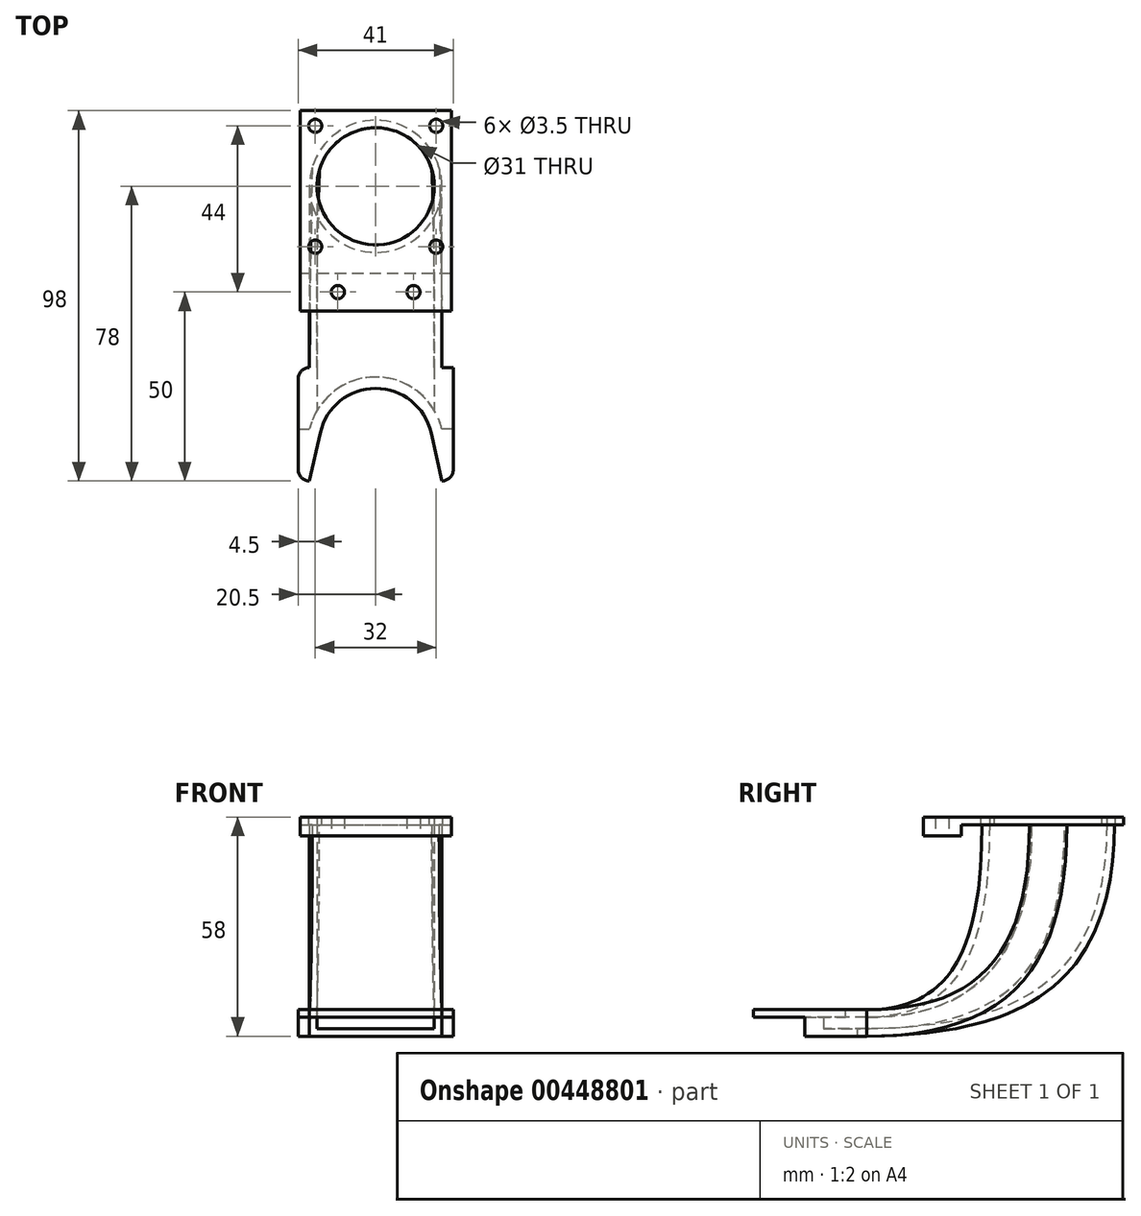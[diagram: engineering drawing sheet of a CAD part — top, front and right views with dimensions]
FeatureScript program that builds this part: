
annotation { "Feature Type Name" : "Feature", "Feature Type Description" : "" }
export const myFeature = defineFeature(function(context is Context, id is Id, definition is map)
    precondition{}
    {
        {
            var Q0;
            Q0=qCreatedBy(makeId("Top.planeOp"),FACE);
            var sketch = newSketch(context, id + "F0", { "sketchPlane" : qUnion([Q0])});
            skLineSegment(sketch, "E0.bottom", {"start": v(0, 0) * mm, "end": v(-40, 0) * mm});
            skLineSegment(sketch, "E0.top", {"start": v(0, 10) * mm, "end": v(-40, 10) * mm});
            skLineSegment(sketch, "E0.left", {"start": v(0, 0) * mm, "end": v(0, 10) * mm});
            skLineSegment(sketch, "E0.right", {"start": v(-40, 0) * mm, "end": v(-40, 10) * mm});
            skCircle(sketch, "E1", {"center": v(-30, 5) * mm, "radius": 1.75 * mm});
            skPoint(sketch, "E1.centerSnap0", {"position": v(-40, 5) * mm});
            skCircle(sketch, "E2", {"center": v(-10, 5) * mm, "radius": 1.75 * mm});
            skPoint(sketch, "E2.centerSnap0", {"position": v(0, 5) * mm});
            skSolve(sketch);
        }
        {
            var Q0;
            Q0=makeQuery(id+"F0.imprint","IMPRINT",FACE,{"disambiguationData":[TD([[makeQuery(id+"F0.imprint","IMPRINT",EDGE,{"derivedFrom":sQuery(id+"F0.wireOp",EDGE,"E0.bottom")}),-1.0]])]});
            extrude(context, id + "F1", {"entities" : qUnion([Q0]), "depth" : 5 * mm});
        }
        {
            var Q0;
            Q0=makeQuery(id+"F1.opExtrude","SWEPT_FACE",FACE,{"disambiguationData":[OSD([sQuery(id+"F0.wireOp",EDGE,"E0.top")])]});
            var sketch = newSketch(context, id + "F2", { "sketchPlane" : qUnion([Q0])});
            skLineSegment(sketch, "E3.bottom", {"start": v(40, 5) * mm, "end": v(0, 5) * mm});
            skLineSegment(sketch, "E3.top", {"start": v(40, 3) * mm, "end": v(0, 3) * mm});
            skLineSegment(sketch, "E3.left", {"start": v(40, 5) * mm, "end": v(40, 3) * mm});
            skLineSegment(sketch, "E3.right", {"start": v(0, 5) * mm, "end": v(0, 3) * mm});
            skSolve(sketch);
        }
        {
            var Q0;
            Q0=makeQuery(id+"F2.imprint","IMPRINT",FACE,{"disambiguationData":[TD([[makeQuery(id+"F2.imprint","IMPRINT",EDGE,{"derivedFrom":sQuery(id+"F2.wireOp",EDGE,"E3.bottom")}),-1.0]])]});
            extrude(context, id + "F3", {"entities" : qUnion([Q0]), "operationType" : NewBodyOperationType.ADD, "depth" : 43 * mm});
        }
        {
            var Q0;
            Q0=makeQuery(id+"F3.boolean.opBoolean","MERGE",FACE,{"derivedFrom":[makeQuery(id+"F1.opExtrude","CAP_FACE",FACE,{"disambiguationData":[OSD([sQuery(id+"F0.wireOp",EDGE,"E0.bottom"),sQuery(id+"F0.wireOp",EDGE,"E0.top"),sQuery(id+"F0.wireOp",EDGE,"E0.left"),sQuery(id+"F0.wireOp",EDGE,"E0.right"),sQuery(id+"F0.wireOp",EDGE,"E1"),sQuery(id+"F0.wireOp",EDGE,"E2")])],"isStart":false}),makeQuery(id+"F3.opExtrude","SWEPT_FACE",FACE,{"disambiguationData":[OSD([sQuery(id+"F2.wireOp",EDGE,"E3.bottom")])]})]});
            var sketch = newSketch(context, id + "F4", { "sketchPlane" : qUnion([Q0])});
            skLineSegment(sketch, "E4.bottom", {"start": v(-36, 49) * mm, "end": v(-4, 49) * mm, "construction": true});
            skLineSegment(sketch, "E4.top", {"start": v(-36, 17) * mm, "end": v(-4, 17) * mm, "construction": true});
            skLineSegment(sketch, "E4.left", {"start": v(-36, 49) * mm, "end": v(-36, 17) * mm, "construction": true});
            skLineSegment(sketch, "E4.right", {"start": v(-4, 49) * mm, "end": v(-4, 17) * mm, "construction": true});
            skPoint(sketch, "E5", {"position": v(-20, 49) * mm});
            skPoint(sketch, "E6", {"position": v(-36, 33) * mm});
            skSolve(sketch);
        }
        {
            var Q0;
            Q0=sQuery(id+"F4.wireOp",VERTEX,"E4.bottom.start");
            var Q1;
            Q1=sQuery(id+"F4.wireOp",VERTEX,"E4.left.end");
            var Q2;
            Q2=sQuery(id+"F4.wireOp",VERTEX,"E4.right.end");
            var Q3;
            Q3=sQuery(id+"F4.wireOp",VERTEX,"E4.right.start");
            var Q4;
            Q4=makeQuery(id+"F1.opExtrude","SWEPT_BODY",BODY,{"disambiguationData":[OSD([sQuery(id+"F0.wireOp",EDGE,"E0.bottom"),sQuery(id+"F0.wireOp",EDGE,"E0.top"),sQuery(id+"F0.wireOp",EDGE,"E0.left"),sQuery(id+"F0.wireOp",EDGE,"E0.right"),sQuery(id+"F0.wireOp",EDGE,"E1"),sQuery(id+"F0.wireOp",EDGE,"E2")])]});
            hole(context, id + "F5", {"style" : HoleStyle.SIMPLE, "endStyle" : HoleEndStyle.THROUGH, "holeDiameter" : 3.5 * mm, "tappedDepth" : 12 * mm, "tapClearance" : 3, "locations" : qUnion([Q0, Q1, Q2, Q3]), "scope" : qUnion([Q4])});
        }
        {
            var Q0;
            Q0=makeQuery(id+"F3.boolean.opBoolean","MERGE",FACE,{"derivedFrom":[makeQuery(id+"F1.opExtrude","CAP_FACE",FACE,{"disambiguationData":[OSD([sQuery(id+"F0.wireOp",EDGE,"E0.bottom"),sQuery(id+"F0.wireOp",EDGE,"E0.top"),sQuery(id+"F0.wireOp",EDGE,"E0.left"),sQuery(id+"F0.wireOp",EDGE,"E0.right"),sQuery(id+"F0.wireOp",EDGE,"E1"),sQuery(id+"F0.wireOp",EDGE,"E2")])],"isStart":false}),makeQuery(id+"F3.opExtrude","SWEPT_FACE",FACE,{"disambiguationData":[OSD([sQuery(id+"F2.wireOp",EDGE,"E3.bottom")])]})]});
            var sketch = newSketch(context, id + "F6", { "sketchPlane" : qUnion([Q0])});
            skCircle(sketch, "E7", {"center": v(-20, 33) * mm, "radius": 17.5 * mm});
            skLineSegment(sketch, "E8", {"start": v(-36, 17) * mm, "end": v(-36, 49) * mm, "construction": true});
            skPoint(sketch, "E9", {"position": v(-36, 33) * mm});
            skSolve(sketch);
        }
        {
            var Q0;
            Q0=makeQuery(id+"F6.imprint","IMPRINT",FACE,{"disambiguationData":[TD([[makeQuery(id+"F6.imprint","IMPRINT",EDGE,{"derivedFrom":sQuery(id+"F6.wireOp",EDGE,"E7")}),1.0]])]});
            extrude(context, id + "F7", {"entities" : qUnion([Q0]), "operationType" : NewBodyOperationType.REMOVE, "endBound" : BoundingType.THROUGH_ALL, "oppositeDirection" : true, "depth" : 25 * mm});
        }
        {
            var Q0;
            Q0=makeQuery(id+"F3.opExtrude","SWEPT_FACE",FACE,{"disambiguationData":[OSD([sQuery(id+"F2.wireOp",EDGE,"E3.top")])]});
            var sketch = newSketch(context, id + "F8", { "sketchPlane" : qUnion([Q0])});
            skSolve(sketch);
        }
        {
            var Q0;
            Q0=makeQuery(id+"F1.opExtrude","SWEPT_FACE",FACE,{"disambiguationData":[OSD([sQuery(id+"F0.wireOp",EDGE,"E0.bottom")])]});
            cPlane(context, id + "F9", {"entities" : qUnion([Q0]), "cplaneType" : CPlaneType.OFFSET, "offset" : 45 * mm, "width" : 150 * mm, "height" : 150 * mm});
        }
        {
            var Q0;
            Q0=qCreatedBy(id+"F9.planeOp",FACE);
            var sketch = newSketch(context, id + "F10", { "sketchPlane" : qUnion([Q0])});
            skLineSegment(sketch, "E10.bottom", {"start": v(-37.5, -53) * mm, "end": v(-2.5, -53) * mm});
            skLineSegment(sketch, "E10.top", {"start": v(-37.5, -46) * mm, "end": v(-2.5, -46) * mm});
            skLineSegment(sketch, "E10.left", {"start": v(-37.5, -53) * mm, "end": v(-37.5, -46) * mm});
            skLineSegment(sketch, "E10.right", {"start": v(-2.5, -53) * mm, "end": v(-2.5, -46) * mm});
            skPoint(sketch, "E11", {"position": v(-20, -46) * mm});
            skSolve(sketch);
        }
        {
            var Q0;
            Q0=makeQuery(id+"F10.imprint","IMPRINT",FACE,{"disambiguationData":[TD([[makeQuery(id+"F10.imprint","IMPRINT",EDGE,{"derivedFrom":sQuery(id+"F10.wireOp",EDGE,"E10.bottom")}),1.0]])]});
            extrude(context, id + "F11", {"entities" : qUnion([Q0]), "oppositeDirection" : true, "depth" : 30 * mm});
        }
        {
            var Q0;
            {var subQ0=sQuery(id+"F2.wireOp",EDGE,"E3.top");Q0=makeQuery(id+"F8.imprint","IMPRINT",FACE,{"disambiguationData":[TD([[makeQuery(id+"F8.imprint","IMPRINT",EDGE,{"derivedFrom":makeQuery(id+"F3.opExtrude","CAP_EDGE",EDGE,{"disambiguationData":[OSD([subQ0])],"isStart":false})}),1.0]])]});}
            var sketch = newSketch(context, id + "F12", { "sketchPlane" : qUnion([Q0])});
            skArc(sketch, "E12", {"start": v(-3.21, -28.05) * mm, "mid": v(-20, -15.5) * mm, "end": v(-36.79, -28.05) * mm});
            skArc(sketch, "E13", {"start": v(-36.79, -37.95) * mm, "mid": v(-20, -50.5) * mm, "end": v(-3.21, -37.95) * mm});
            skArc(sketch, "E14", {"start": v(-36.79, -28.05) * mm, "mid": v(-37.5, -33) * mm, "end": v(-36.79, -37.95) * mm});
            skArc(sketch, "E15", {"start": v(-3.21, -37.95) * mm, "mid": v(-2.5, -33) * mm, "end": v(-3.21, -28.05) * mm});
            skLineSegment(sketch, "E16", {"start": v(-36.79, -28.05) * mm, "end": v(-3.21, -37.95) * mm, "construction": true});
            skLineSegment(sketch, "E17", {"start": v(-3.21, -28.05) * mm, "end": v(-36.79, -37.95) * mm, "construction": true});
            skLineSegment(sketch, "E18", {"start": v(-2.5, -33) * mm, "end": v(-37.5, -33) * mm, "construction": true});
            skSolve(sketch);
        }
        {
            var Q1;
            Q1=qSketchRegion(id+"F12",true);
            var Q2;
            Q2=makeQuery(id+"F11.opExtrude","CAP_FACE",FACE,{"disambiguationData":[OSD([sQuery(id+"F10.wireOp",EDGE,"E10.bottom"),sQuery(id+"F10.wireOp",EDGE,"E10.top"),sQuery(id+"F10.wireOp",EDGE,"E10.left"),sQuery(id+"F10.wireOp",EDGE,"E10.right")])],"isStart":false});
            var Q3;
            Q3=sQuery(id+"FFYjmbXSwY1wBhW_2.wireOp",VERTEX,"5CUcN9Ah-aoQc-i0Y4-lSSF-3NxKRFAfKakx.start");
            var Q4;
            Q4=sQuery(id+"FFYjmbXSwY1wBhW_2.wireOp",VERTEX,"9UqwaanU-PZ8O-Q84W-1Uu3-IYepP7ym5t6i.end");
            var Q5;
            Q5=sQuery(id+"FFYjmbXSwY1wBhW_2.wireOp",VERTEX,"3rHOv9Gl-2p6t-3ORE-IPYh-5aPjCGt6IKt6.end");
            var Q6;
            Q6=sQuery(id+"FFYjmbXSwY1wBhW_2.wireOp",VERTEX,"h81LCoKd-EBxs-FelB-gbCS-DPIwCHQTHsDM.start");
            loft(context, id + "F13", {"operationType" : NewBodyOperationType.ADD, "startCondition" : LoftEndDerivativeType.NORMAL_TO_PROFILE, "startMagnitude" : 2, "endCondition" : LoftEndDerivativeType.NORMAL_TO_PROFILE, "endMagnitude" : 2, "sheetProfilesArray" : [{ "sheetProfileEntities" : qUnion([Q1]) }, { "sheetProfileEntities" : qUnion([Q2]) }], "connections" : [{ "connectionEntities" : qUnion([Q3, Q4, Q5, Q6]), "connectionEdgeQueries" : qUnion([]), "connectionEdgeParameters" : [] }]});
        }
        {
            var Q0;
            Q0=makeQuery(id+"F13.opLoft","CAP_FACE",FACE,{"disambiguationData":[OSD([makeQuery(id+"F12.imprint","IMPRINT",FACE,{"disambiguationData":[TD([[makeQuery(id+"F12.imprint","IMPRINT",EDGE,{"derivedFrom":sQuery(id+"F12.wireOp",EDGE,"E12")}),1.0]])]})])],"isStart":true});
            shell(context, id + "F14", {"entities" : qUnion([Q0]), "thickness" : 2 * mm});
        }
        {
            var Q0;
            Q0=makeQuery(id+"F11.opExtrude","SWEPT_FACE",FACE,{"disambiguationData":[OSD([sQuery(id+"F10.wireOp",EDGE,"E10.top")])]});
            var sketch = newSketch(context, id + "F15", { "sketchPlane" : qUnion([Q0])});
            skArc(sketch, "E19", {"start": v(-5.36, -32.22) * mm, "mid": v(-20, -20.5) * mm, "end": v(-34.64, -32.22) * mm});
            skPoint(sketch, "E19.centerSnap0", {"position": v(-20, -45) * mm});
            skLineSegment(sketch, "E20", {"start": v(-2.5, -45) * mm, "end": v(-5.36, -32.22) * mm});
            skLineSegment(sketch, "E21", {"start": v(-37.5, -45) * mm, "end": v(-34.64, -32.22) * mm});
            skLineSegment(sketch, "E22", {"start": v(-37.5, -45) * mm, "end": v(-2.5, -45) * mm});
            skSolve(sketch);
        }
        {
            var Q0;
            Q0=makeQuery(id+"F15.imprint","IMPRINT",FACE,{"disambiguationData":[TD([[makeQuery(id+"F15.imprint","IMPRINT",EDGE,{"derivedFrom":sQuery(id+"F15.wireOp",EDGE,"E19")}),1.0]])]});
            extrude(context, id + "F16", {"entities" : qUnion([Q0]), "operationType" : NewBodyOperationType.REMOVE, "endBound" : BoundingType.THROUGH_ALL, "oppositeDirection" : true, "depth" : 25 * mm});
        }
        {
            var Q0;
            Q0=makeQuery(id+"F11.opExtrude","SWEPT_FACE",FACE,{"disambiguationData":[OSD([sQuery(id+"F10.wireOp",EDGE,"E10.bottom")])]});
            var sketch = newSketch(context, id + "F17", { "sketchPlane" : qUnion([Q0])});
            skArc(sketch, "E23", {"start": v(-37.5, 31.29) * mm, "mid": v(-20, 17.5) * mm, "end": v(-2.5, 31.29) * mm});
            skLineSegment(sketch, "E24", {"start": v(-37.5, 45) * mm, "end": v(-37.5, 31.29) * mm});
            skPoint(sketch, "E24.endSnap0", {"position": v(-37.5, 30) * mm});
            skLineSegment(sketch, "E25", {"start": v(-2.5, 45) * mm, "end": v(-2.5, 31.29) * mm});
            skLineSegment(sketch, "E26", {"start": v(-2.5, 45) * mm, "end": v(-37.5, 45) * mm});
            skSolve(sketch);
        }
        {
            var Q0;
            {var subQ1=sQuery(id+"F10.wireOp",EDGE,"E10.bottom");var subQ2=makeQuery(id+"F11.opExtrude","SWEPT_FACE",FACE,{"disambiguationData":[OSD([subQ1])]});var subQ6=makeQuery(id+"F16.opExtrude","SWEPT_FACE",FACE,{"disambiguationData":[OSD([sQuery(id+"F15.wireOp",EDGE,"E19")])]});var subQ12=makeQuery(id+"F16.boolean.opBoolean","INTERSECT",EDGE,{"derivedFrom":[subQ2,subQ6]});Q0=makeQuery(id+"F17.imprint","IMPRINT",FACE,{"disambiguationData":[TD([[makeQuery(id+"F17.imprint","IMPRINT",EDGE,{"derivedFrom":subQ12}),-1.0]])]});}
            var Q1;
            Q1=makeQuery(id+"F14.opShell","OFFSET_FACE",FACE,{"disambiguationData":[OSD([sQuery(id+"F10.wireOp",EDGE,"E10.top")])]});
            extrude(context, id + "F18", {"entities" : qUnion([Q0]), "operationType" : NewBodyOperationType.REMOVE, "endBound" : BoundingType.UP_TO_SURFACE, "oppositeDirection" : true, "endBoundEntityFace" : qUnion([Q1]), "depth" : 25 * mm});
        }
        {
            var Q0;
            Q0=makeQuery(id+"F8.imprint","IMPRINT",FACE,{"disambiguationData":[TD([[makeQuery(id+"F8.imprint","IMPRINT",EDGE,{"derivedFrom":makeQuery(id+"F7.boolean.opBoolean","INTERSECT",EDGE,{"derivedFrom":[makeQuery(id+"F3.opExtrude","SWEPT_FACE",FACE,{"disambiguationData":[OSD([sQuery(id+"F2.wireOp",EDGE,"E3.top")])]}),makeQuery(id+"F7.opExtrude","SWEPT_FACE",FACE,{"disambiguationData":[OSD([sQuery(id+"F6.wireOp",EDGE,"E7")])]})]})}),1.0]])]});
            var sketch = newSketch(context, id + "F19", { "sketchPlane" : qUnion([Q0])});
            skCircle(sketch, "E27", {"center": v(-20, -33) * mm, "radius": 17.5 * mm});
            skCircle(sketch, "E28", {"center": v(-20, -33) * mm, "radius": 15.5 * mm});
            skSolve(sketch);
        }
        {
            var Q0;
            Q0=makeQuery(id+"F19.imprint","IMPRINT",FACE,{"disambiguationData":[TD([[makeQuery(id+"F19.imprint","IMPRINT",EDGE,{"derivedFrom":sQuery(id+"F19.wireOp",EDGE,"E27")}),1.0]])]});
            var Q1;
            Q1=makeQuery(id+"F3.boolean.opBoolean","MERGE",FACE,{"derivedFrom":[makeQuery(id+"F1.opExtrude","CAP_FACE",FACE,{"disambiguationData":[OSD([sQuery(id+"F0.wireOp",EDGE,"E0.bottom"),sQuery(id+"F0.wireOp",EDGE,"E0.top"),sQuery(id+"F0.wireOp",EDGE,"E0.left"),sQuery(id+"F0.wireOp",EDGE,"E0.right"),sQuery(id+"F0.wireOp",EDGE,"E1"),sQuery(id+"F0.wireOp",EDGE,"E2")])],"isStart":false}),makeQuery(id+"F3.opExtrude","SWEPT_FACE",FACE,{"disambiguationData":[OSD([sQuery(id+"F2.wireOp",EDGE,"E3.bottom")])]})]});
            extrude(context, id + "F20", {"entities" : qUnion([Q0]), "operationType" : NewBodyOperationType.ADD, "endBound" : BoundingType.UP_TO_SURFACE, "oppositeDirection" : true, "endBoundEntityFace" : qUnion([Q1]), "depth" : 25 * mm});
        }
        {
            var Q0;
            Q0=makeQuery(id+"F11.opExtrude","SWEPT_FACE",FACE,{"disambiguationData":[OSD([sQuery(id+"F10.wireOp",EDGE,"E10.left")])]});
            var sketch = newSketch(context, id + "F24", { "sketchPlane" : qUnion([Q0])});
            skLineSegment(sketch, "E29.bottom", {"start": v(15, -46) * mm, "end": v(45, -46) * mm});
            skLineSegment(sketch, "E29.top", {"start": v(15, -53) * mm, "end": v(45, -53) * mm});
            skLineSegment(sketch, "E29.left", {"start": v(15, -46) * mm, "end": v(15, -53) * mm});
            skLineSegment(sketch, "E29.right", {"start": v(45, -46) * mm, "end": v(45, -53) * mm});
            skSolve(sketch);
        }
        {
            var Q0;
            {var subQ1=sQuery(id+"F17.wireOp",EDGE,"E24");var subQ5=makeQuery(id+"F18.boolean.opBoolean","COPY",EDGE,{"derivedFrom":makeQuery(id+"F18.opExtrude","TWEAK_EDGE",EDGE,{"derivedFrom":[makeQuery(id+"F14.opShell","OFFSET_FACE",FACE,{"disambiguationData":[OSD([sQuery(id+"F10.wireOp",EDGE,"E10.top")])]}),makeQuery(id+"F17.imprint","IMPRINT",EDGE,{"derivedFrom":subQ1})]})});Q0=makeQuery(id+"F24.imprint","IMPRINT",FACE,{"disambiguationData":[TD([[makeQuery(id+"F24.imprint","IMPRINT",EDGE,{"derivedFrom":subQ5}),1.0]])]});}
            var Q1;
            {var subQ2=sQuery(id+"F24.wireOp",EDGE,"E29.bottom");Q1=makeQuery(id+"F24.imprint","IMPRINT",FACE,{"disambiguationData":[TD([[makeQuery(id+"F24.imprint","IMPRINT",EDGE,{"derivedFrom":subQ2}),-1.0]])]});}
            extrude(context, id + "F21", {"entities" : qUnion([Q0, Q1]), "operationType" : NewBodyOperationType.ADD, "depth" : 3 * mm});
        }
        {
            var Q0;
            Q0=makeQuery(id+"F11.opExtrude","SWEPT_FACE",FACE,{"disambiguationData":[OSD([sQuery(id+"F10.wireOp",EDGE,"E10.right")])]});
            var sketch = newSketch(context, id + "F22", { "sketchPlane" : qUnion([Q0])});
            skLineSegment(sketch, "E30.bottom", {"start": v(-15, -53) * mm, "end": v(-45, -53) * mm});
            skLineSegment(sketch, "E30.top", {"start": v(-15, -46) * mm, "end": v(-45, -46) * mm});
            skLineSegment(sketch, "E30.left", {"start": v(-15, -53) * mm, "end": v(-15, -46) * mm});
            skLineSegment(sketch, "E30.right", {"start": v(-45, -53) * mm, "end": v(-45, -46) * mm});
            skSolve(sketch);
        }
        {
            var Q0;
            {var subQ1=sQuery(id+"F22.wireOp",EDGE,"E30.top");Q0=makeQuery(id+"F22.imprint","IMPRINT",FACE,{"disambiguationData":[TD([[makeQuery(id+"F22.imprint","IMPRINT",EDGE,{"derivedFrom":subQ1}),1.0]])]});}
            var Q1;
            {var subQ1=sQuery(id+"F17.wireOp",EDGE,"E25");var subQ5=makeQuery(id+"F18.boolean.opBoolean","COPY",EDGE,{"derivedFrom":makeQuery(id+"F18.opExtrude","TWEAK_EDGE",EDGE,{"derivedFrom":[makeQuery(id+"F14.opShell","OFFSET_FACE",FACE,{"disambiguationData":[OSD([sQuery(id+"F10.wireOp",EDGE,"E10.top")])]}),makeQuery(id+"F17.imprint","IMPRINT",EDGE,{"derivedFrom":subQ1})]})});Q1=makeQuery(id+"F22.imprint","IMPRINT",FACE,{"disambiguationData":[TD([[makeQuery(id+"F22.imprint","IMPRINT",EDGE,{"derivedFrom":subQ5}),-1.0]])]});}
            extrude(context, id + "F23", {"entities" : qUnion([Q0, Q1]), "operationType" : NewBodyOperationType.ADD, "depth" : 3 * mm});
        }
        {
            var Q0;
            Q0=makeQuery(id+"F23.opExtrude","CAP_EDGE",EDGE,{"disambiguationData":[OSD([sQuery(id+"F22.wireOp",EDGE,"E30.right")])],"isStart":false});
            var Q1;
            Q1=makeQuery(id+"F21.opExtrude","CAP_EDGE",EDGE,{"disambiguationData":[OSD([sQuery(id+"F24.wireOp",EDGE,"E29.right")])],"isStart":false});
            var Q2;
            Q2=makeQuery(id+"F21.opExtrude","CAP_EDGE",EDGE,{"disambiguationData":[OSD([sQuery(id+"F24.wireOp",EDGE,"E29.left")])],"isStart":false});
            fillet(context, id + "F25", {"entities" : qUnion([Q0, Q1, Q2]), "radius" : 3 * mm, "tangentPropagation" : true, "allowEdgeOverflow" : false});
        }
    });
